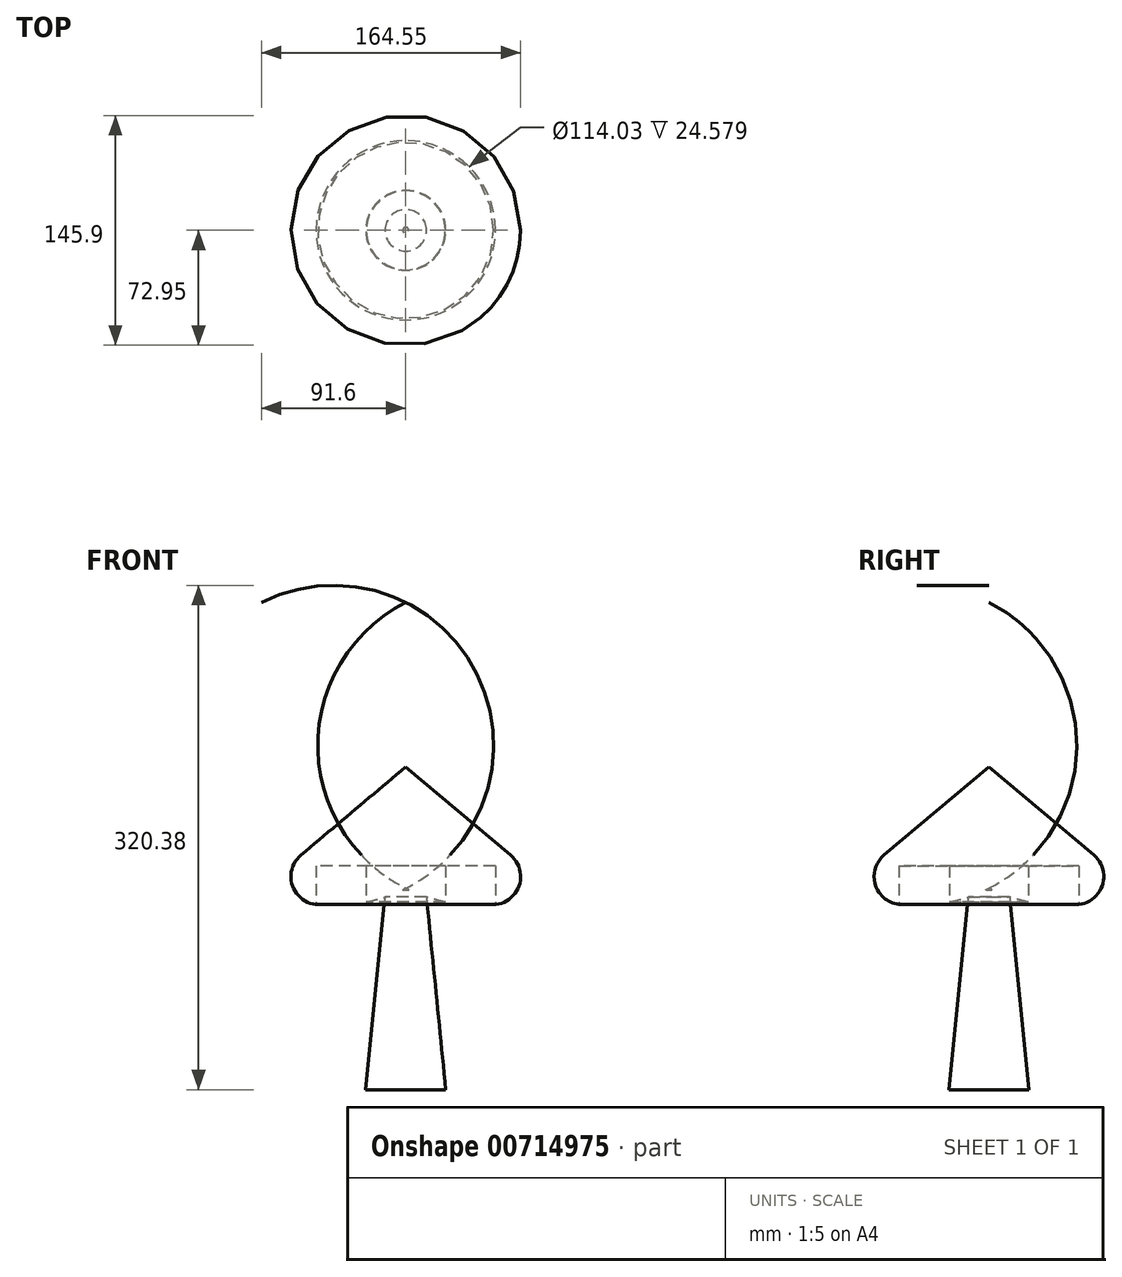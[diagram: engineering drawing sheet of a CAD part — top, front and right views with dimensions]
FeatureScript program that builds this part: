
annotation { "Feature Type Name" : "Feature", "Feature Type Description" : "" }
export const myFeature = defineFeature(function(context is Context, id is Id, definition is map)
    precondition{}
    {
        {
            var Q0;
            Q0=qCreatedBy(makeId("Top.planeOp"),FACE);
            var sketch = newSketch(context, id + "F0", { "sketchPlane" : qUnion([Q0])});
            skCircle(sketch, "E0", {"center": v(0, 0) * mm, "radius": 25.4 * mm});
            skSolve(sketch);
        }
        {
            var Q0;
            Q0=qCreatedBy(makeId("Top.planeOp"),FACE);
            cPlane(context, id + "F1", {"entities" : qUnion([Q0]), "cplaneType" : CPlaneType.OFFSET, "offset" : 127 * mm, "width" : 152.4 * mm, "height" : 152.4 * mm});
        }
        {
            var Q0;
            Q0=qCreatedBy(id+"F1.planeOp",FACE);
            var sketch = newSketch(context, id + "F2", { "sketchPlane" : qUnion([Q0])});
            skCircle(sketch, "E1", {"center": v(0, 0) * mm, "radius": 12.7 * mm});
            skSolve(sketch);
        }
        {
            var Q0;
            Q0=makeQuery(id+"F0.imprint","IMPRINT",FACE,{"disambiguationData":[TD([[makeQuery(id+"F0.imprint","IMPRINT",EDGE,{"derivedFrom":sQuery(id+"F0.wireOp",EDGE,"E0")}),1.0]])]});
            var Q1;
            Q1=makeQuery(id+"F2.imprint","IMPRINT",FACE,{"disambiguationData":[TD([[makeQuery(id+"F2.imprint","IMPRINT",EDGE,{"derivedFrom":sQuery(id+"F2.wireOp",EDGE,"E1")}),1.0]])]});
            loft(context, id + "F3", {"sheetProfilesArray" : [{ "sheetProfileEntities" : qUnion([Q0]) }, { "sheetProfileEntities" : qUnion([Q1]) }]});
        }
        {
            var Q0;
            Q0=qCreatedBy(makeId("Front.planeOp"),FACE);
            var sketch = newSketch(context, id + "F4", { "sketchPlane" : qUnion([Q0])});
            skLineSegment(sketch, "E2", {"start": v(0, 127.94) * mm, "end": v(0, 204.96) * mm});
            skLineSegment(sketch, "E3", {"start": v(0, 204.96) * mm, "end": v(-91.6, 127.94) * mm});
            skArc(sketch, "E4", {"start": v(-91.6, 127.94) * mm, "mid": v(-45.8, 117.04) * mm, "end": v(0, 127.94) * mm});
            skSolve(sketch);
        }
        {
            var Q0;
            Q0 = qSketchRegion(id + "F4", true);
            var Q1;
            Q1=sQuery(id+"F4.wireOp",EDGE,"E2");
            revolve(context, id + "F5", {"operationType" : NewBodyOperationType.ADD, "surfaceOperationType" : NewSurfaceOperationType.NEW, "entities" : qUnion([Q0]), "axis" : qUnion([Q1]), "revolveType" : RevolveType.FULL});
        }
        {
            var Q0;
            Q0=makeQuery(id+"F5.opRevolve","SWEPT_FACE",FACE,{"disambiguationData":[OSD([sQuery(id+"F4.wireOp",EDGE,"E3")])]});
            fillet(context, id + "F6", {"entities" : qUnion([Q0]), "radius" : 17.78 * mm, "tangentPropagation" : true, "allowEdgeOverflow" : false});
        }
        {
            var Q0;
            Q0=qCreatedBy(makeId("Top.planeOp"),FACE);
            cPlane(context, id + "F7", {"entities" : qUnion([Q0]), "cplaneType" : CPlaneType.OFFSET, "offset" : 116.84 * mm, "width" : 152.4 * mm, "height" : 152.4 * mm});
        }
        {
            var Q0;
            Q0=qCreatedBy(id+"F7.planeOp",FACE);
            var sketch = newSketch(context, id + "F8", { "sketchPlane" : qUnion([Q0])});
            skCircle(sketch, "E5", {"center": v(0, 0) * mm, "radius": 25.1 * mm});
            skCircle(sketch, "E6", {"center": v(0, 0) * mm, "radius": 57.01 * mm});
            skSolve(sketch);
        }
        {
            var Q0;
            Q0=makeQuery(id+"F8.imprint","IMPRINT",FACE,{"disambiguationData":[TD([[makeQuery(id+"F8.imprint","IMPRINT",EDGE,{"derivedFrom":sQuery(id+"F8.wireOp",EDGE,"E5")}),-1.0]])]});
            extrude(context, id + "F9", {"entities" : qUnion([Q0]), "operationType" : NewBodyOperationType.REMOVE, "depth" : 25.4 * mm, "offsetDistance" : 25.4 * mm});
        }
    });
